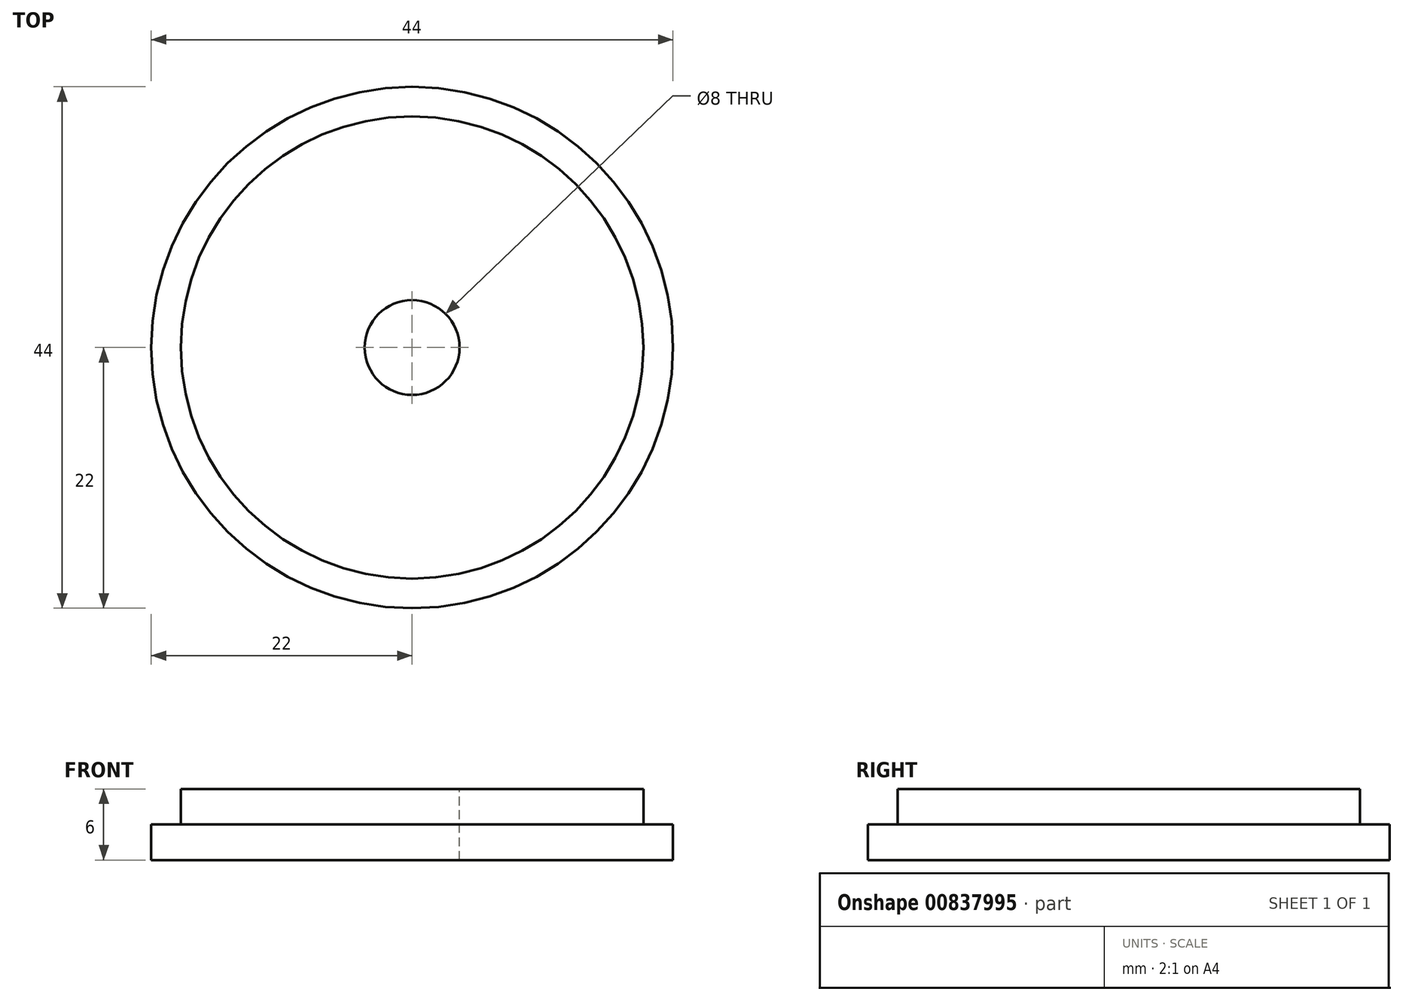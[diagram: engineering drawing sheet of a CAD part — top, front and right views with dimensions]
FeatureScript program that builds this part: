
annotation { "Feature Type Name" : "Feature", "Feature Type Description" : "" }
export const myFeature = defineFeature(function(context is Context, id is Id, definition is map)
    precondition{}
    {
        {
            var Q0;
            Q0=qCreatedBy(makeId("Top.planeOp"),FACE);
            var sketch = newSketch(context, id + "F0", { "sketchPlane" : qUnion([Q0])});
            skCircle(sketch, "E0", {"center": v(0, 0) * mm, "radius": 22 * mm});
            skSolve(sketch);
        }
        {
            var Q0;
            Q0=makeQuery(id+"F0.imprint","IMPRINT",FACE,{"disambiguationData":[TD([[makeQuery(id+"F0.imprint","IMPRINT",EDGE,{"derivedFrom":sQuery(id+"F0.wireOp",EDGE,"E0")}),1.0]])]});
            extrude(context, id + "F1", {"entities" : qUnion([Q0]), "depth" : 3 * mm, "offsetDistance" : 25 * mm});
        }
        {
            var Q0;
            Q0=makeQuery(id+"F1.opExtrude","CAP_FACE",FACE,{"disambiguationData":[OSD([sQuery(id+"F0.wireOp",EDGE,"E0")])],"isStart":false});
            var sketch = newSketch(context, id + "F2", { "sketchPlane" : qUnion([Q0])});
            skCircle(sketch, "E1", {"center": v(0, 0) * mm, "radius": 19.5 * mm});
            skSolve(sketch);
        }
        {
            var Q0;
            Q0 = qSketchRegion(id + "F2", true);
            extrude(context, id + "F3", {"entities" : qUnion([Q0]), "operationType" : NewBodyOperationType.ADD, "depth" : 3 * mm, "offsetDistance" : 25 * mm});
        }
        {
            var Q0;
            Q0=makeQuery(id+"F3.opExtrude","CAP_FACE",FACE,{"disambiguationData":[OSD([sQuery(id+"F2.wireOp",EDGE,"E1")])],"isStart":false});
            var sketch = newSketch(context, id + "F4", { "sketchPlane" : qUnion([Q0])});
            skCircle(sketch, "E2", {"center": v(0, 0) * mm, "radius": 4 * mm});
            skSolve(sketch);
        }
        {
            var Q0;
            Q0 = qSketchRegion(id + "F4", true);
            extrude(context, id + "F5", {"entities" : qUnion([Q0]), "operationType" : NewBodyOperationType.REMOVE, "endBound" : BoundingType.THROUGH_ALL, "oppositeDirection" : true, "depth" : 25 * mm, "offsetDistance" : 25 * mm});
        }
    });
